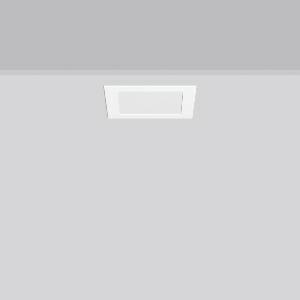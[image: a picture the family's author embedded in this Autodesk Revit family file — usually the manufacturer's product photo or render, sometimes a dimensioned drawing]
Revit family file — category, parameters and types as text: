
# Revit family: toledo_flat_square_e_901486_002_1_d07b
name_source: partatom
category: Lighting Fixtures
units: mm (PartAtom-declared; Revit-internal decimal feet)

## family parameters
Cut with Voids When Loaded = No
Host = Face
Light Source = No
Part Type = Normal
Room Calculation Point = No
Round Connector Dimension = Use Diameter
Shared = No

## types (1)
- TOLEDO FLAT square E (1 x LED Modul 840, 800 lm, 4000)
    Apparent Load = 8 VA
    CIE Flux Codes = 49 80 96 100 100
    Color Rendering = 80
    Color Temperature = 4000
    Default Elevation = 1800 mm
    Description = Series: TOLEDO FLAT square
Ultra thin recessed downlight. Housing: die-cast aluminium. Light guide and diffuser made of non-yellowing PMMA, opal matt. Ceiling installation with spring system. Mounting depth depends on ceiling strength. Suitable for through-wiring with separately available accessories. Surface mounted housing as accessory for all sizes. Retrofittable decorative cylinders made of chintz fabric as accessory, optional with satin finish plastic diffuser. Through-wiring box (5 pole) available as accessory. 
Colour: white
Length: 172 mm
Width: 172 mm
Height: 3 mm
Cut-out length: 156 mm
Cut-out width: 156 mm
Recess height: 28-56 mm
Luminaire: recess height: 31-51 mm
Lamp: LED
Socket: without socket
Colour temperature: 4000K
Colour rendering index (CRI): 80
System power: 8 W
Rated luminous flux: 800 lm
Luminous efficiency: 100 lm/W
Control gear: Regulated power supply
Protection class: II
Type of protection: IP 54
    Height = 0 mm  [stored 0 ft]
    Lamp = 1 x LED Modul 840
    Lamp Light Flux = 800 lm
    Lamp count = 1
    Length = 172 mm
    Lifetime = 50000 h
    Luminous efficacy = 100 lm/W
    Manufacturer = RZB
    ModVariant = No
    Model = 901486.002.1
    Mounting Place = Ceiling
    Mounting Type = Recessed
    Number of Poles = 1
    OnlyDefault = Yes
    Power Factor = 1
    Product Name = TOLEDO FLAT square E
    Product group = Recessed downlights
    ProductGroupID = 402
    Protection Class = Protection class II
    Protection Degree = IP 20
    RLX_Detail_Level = 1
    RLX_Emergency_Light_Flux = 0 lm
    RLX_Emergency_Type = 0
    RLX_Emergency_Type_DB = No
    RlxData = <blob elided: 57885 chars, md5=67c77506>
    Socket = socket
    Standby Power = 0 W
    System Light Flux = 800 lm
    System Power = 8 W
    Type Comments = Product without accessories
    Type Image = 901486.002.jpg
    URL = http://relux.com
    VarID = ---
    Voltage = 230 V
    Voltage Range = 220-240 V
    Weight = 0.00 kg
    Width = 172 mm

note: [stored X ft] marks values corroborated as IEEE doubles in the binary element streams (Revit-internal decimal feet)

## geometry (parser evidence)
native form markers: Blend x4, Sweep x12
no freeform markers — native parametric forms only
